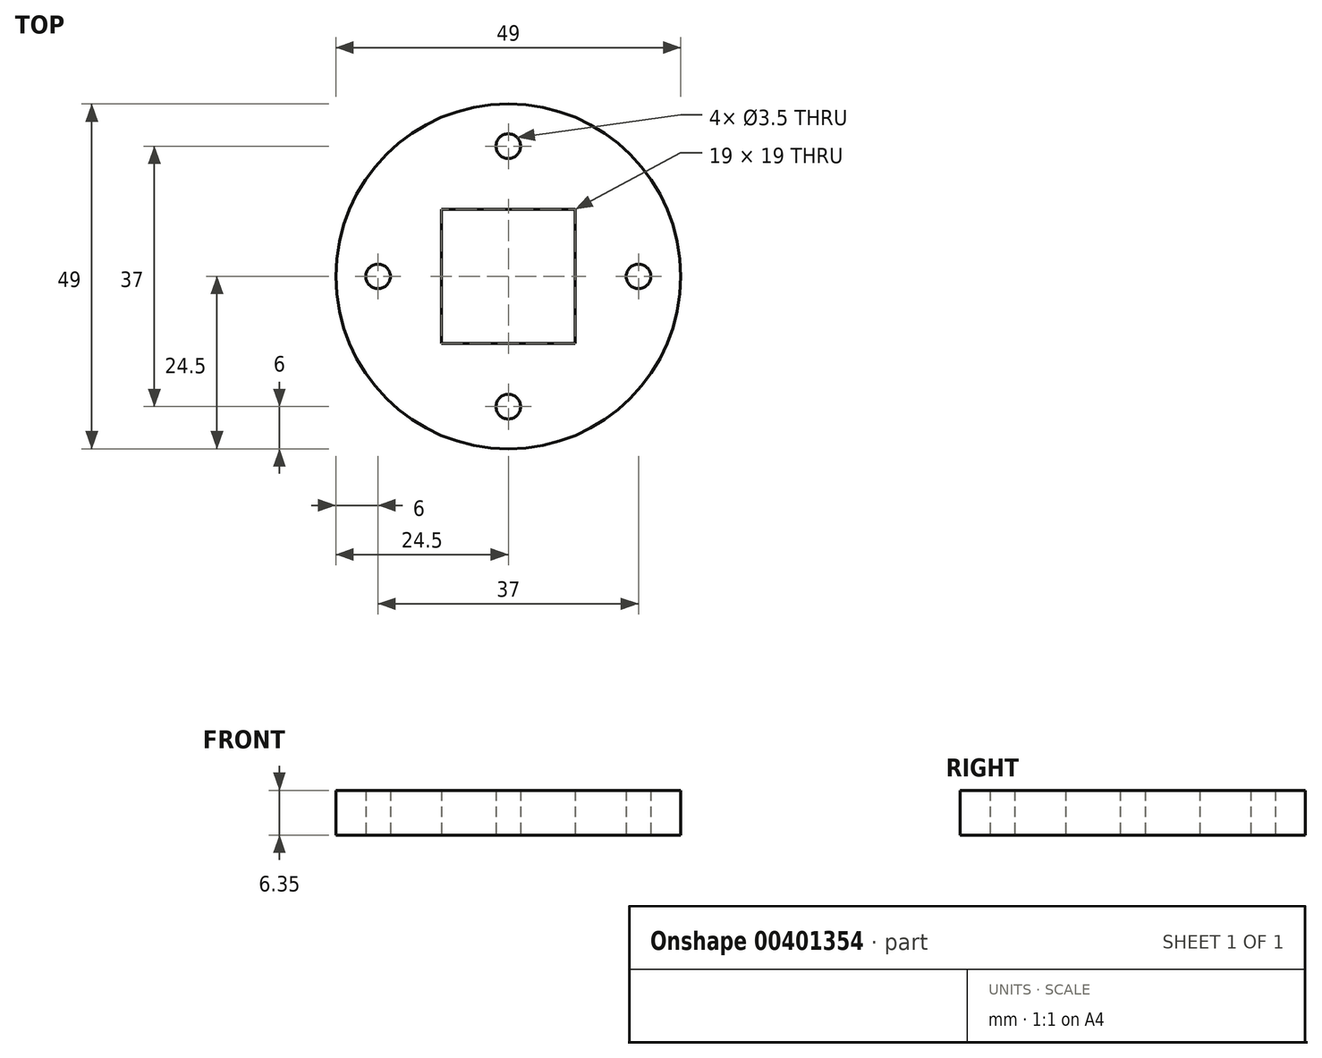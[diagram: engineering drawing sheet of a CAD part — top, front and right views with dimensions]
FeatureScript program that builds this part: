
annotation { "Feature Type Name" : "Feature", "Feature Type Description" : "" }
export const myFeature = defineFeature(function(context is Context, id is Id, definition is map)
    precondition{}
    {
        {
            var Q0;
            Q0=qCreatedBy(makeId("Top.planeOp"),FACE);
            var sketch = newSketch(context, id + "F0", { "sketchPlane" : qUnion([Q0])});
            skCircle(sketch, "E0", {"center": v(0, 0) * mm, "radius": 24.5 * mm});
            skLineSegment(sketch, "E1", {"start": v(0, 24.5) * mm, "end": v(0, -24.5) * mm, "construction": true});
            skLineSegment(sketch, "E2", {"start": v(-24.5, 0) * mm, "end": v(24.5, 0) * mm, "construction": true});
            skCircle(sketch, "E3", {"center": v(-18.5, 0) * mm, "radius": 1.75 * mm});
            skCircle(sketch, "E4", {"center": v(0, 18.5) * mm, "radius": 1.75 * mm});
            skCircle(sketch, "E5", {"center": v(18.5, 0) * mm, "radius": 1.75 * mm});
            skCircle(sketch, "E6", {"center": v(0, -18.5) * mm, "radius": 1.75 * mm});
            skLineSegment(sketch, "E7.bottom", {"start": v(-9.5, 9.5) * mm, "end": v(9.5, 9.5) * mm});
            skLineSegment(sketch, "E7.top", {"start": v(-9.5, -9.5) * mm, "end": v(9.5, -9.5) * mm});
            skLineSegment(sketch, "E7.left", {"start": v(-9.5, 9.5) * mm, "end": v(-9.5, -9.5) * mm});
            skLineSegment(sketch, "E7.right", {"start": v(9.5, 9.5) * mm, "end": v(9.5, -9.5) * mm});
            skSolve(sketch);
        }
        {
            var Q0;
            Q0=makeQuery(id+"F0.imprint","IMPRINT",FACE,{"disambiguationData":[TD([[makeQuery(id+"F0.imprint","IMPRINT",EDGE,{"derivedFrom":sQuery(id+"F0.wireOp",EDGE,"E0")}),1.0]])]});
            extrude(context, id + "F1", {"entities" : qUnion([Q0]), "depth" : 6.35 * mm, "offsetDistance" : 25 * mm});
        }
    });
